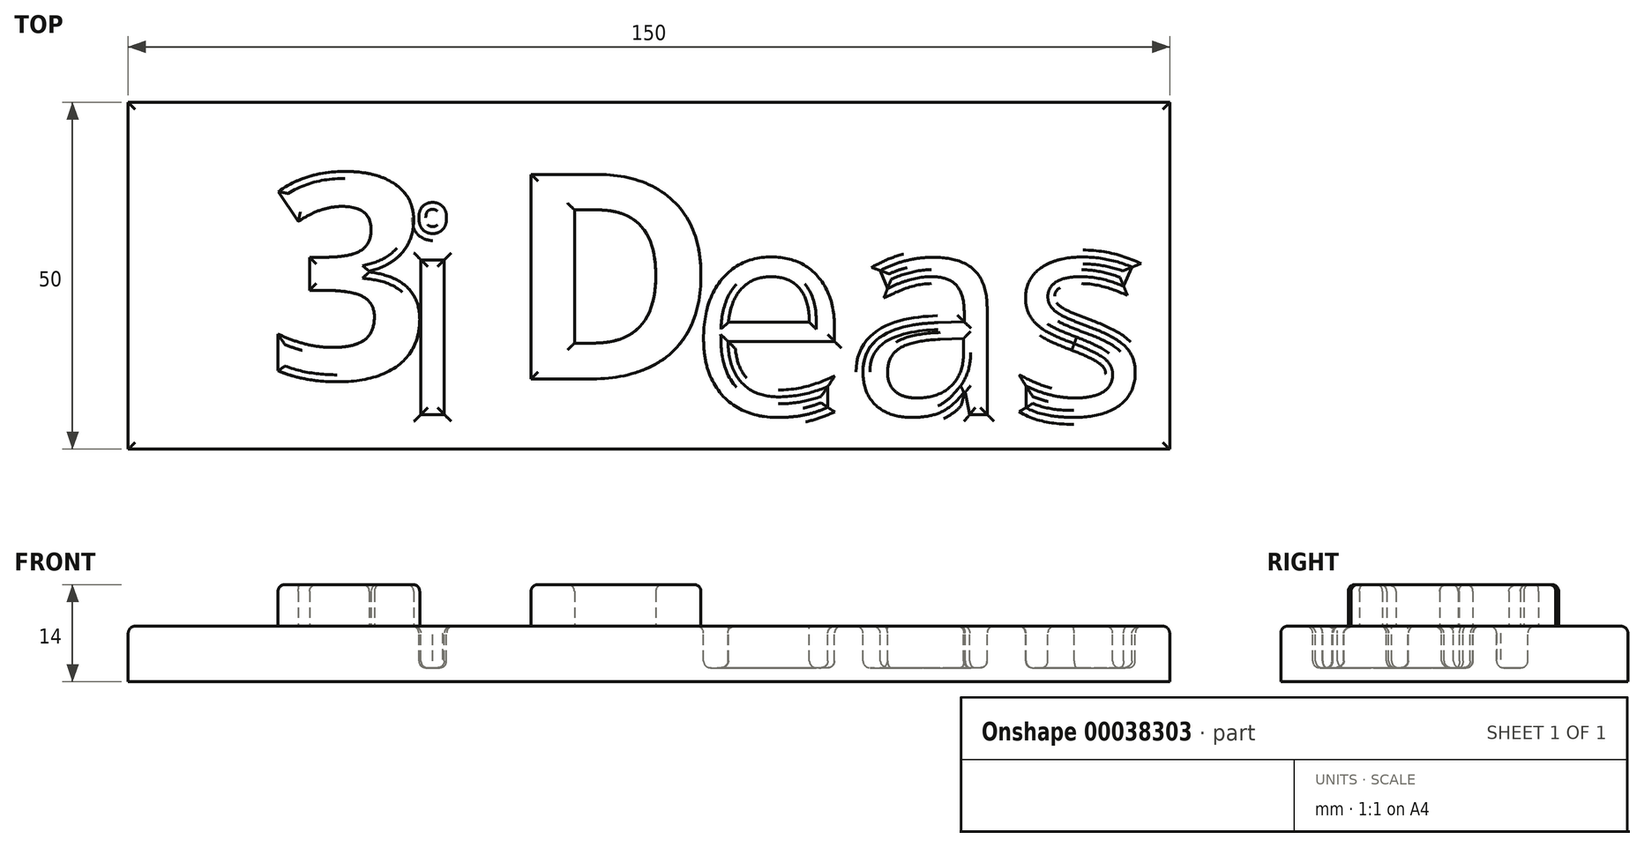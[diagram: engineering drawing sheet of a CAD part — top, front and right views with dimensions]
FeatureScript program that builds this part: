
annotation { "Feature Type Name" : "Feature", "Feature Type Description" : "" }
export const myFeature = defineFeature(function(context is Context, id is Id, definition is map)
    precondition{}
    {
        {
            var Q0;
            Q0=qCreatedBy(makeId("Top.planeOp"),FACE);
            var sketch = newSketch(context, id + "F0", { "sketchPlane" : qUnion([Q0])});
            skLineSegment(sketch, "E0.rect.bottom", {"start": v(-75, 25) * mm, "end": v(75, 25) * mm});
            skLineSegment(sketch, "E0.rect.top", {"start": v(-75, -25) * mm, "end": v(75, -25) * mm});
            skLineSegment(sketch, "E0.rect.left", {"start": v(-75, 25) * mm, "end": v(-75, -25) * mm});
            skLineSegment(sketch, "E0.rect.right", {"start": v(75, 25) * mm, "end": v(75, -25) * mm});
            skPoint(sketch, "E0.rect.middle", {"position": v(0, 0) * mm});
            skSolve(sketch);
        }
        {
            var Q0;
            Q0 = qSketchRegion(id + "F0", true);
            extrude(context, id + "F1", {"entities" : qUnion([Q0]), "depth" : 8 * mm});
        }
        {
            var Q0;
            Q0=makeQuery(id+"F1.opExtrude","CAP_FACE",FACE,{"disambiguationData":[OSD([sQuery(id+"F0.wireOp",EDGE,"E0.rect.bottom"),sQuery(id+"F0.wireOp",EDGE,"E0.rect.top"),sQuery(id+"F0.wireOp",EDGE,"E0.rect.left"),sQuery(id+"F0.wireOp",EDGE,"E0.rect.right")])],"isStart":false});
            var sketch = newSketch(context, id + "F2", { "sketchPlane" : qUnion([Q0])});
            skText(sketch, "E1", { "text": "3 D", "fontName": "OpenSans-Bold.ttf"});
            skPoint(sketch, "E2", {"position": v(-70, 0) * mm});
            const initialGuessF2  = {"E1": [-0.055, -0.01487, 1, 0, 0.02974]};
            skSetInitialGuess(sketch, initialGuessF2);
            skSolve(sketch);
        }
        {
            var Q0;
            Q0 = qSketchRegion(id + "F2", true);
            extrude(context, id + "F3", {"entities" : qUnion([Q0]), "depth" : 6 * mm});
        }
        {
            var Q0;
            Q0=makeQuery(id+"F1.opExtrude","CAP_FACE",FACE,{"disambiguationData":[OSD([sQuery(id+"F0.wireOp",EDGE,"E0.rect.bottom"),sQuery(id+"F0.wireOp",EDGE,"E0.rect.top"),sQuery(id+"F0.wireOp",EDGE,"E0.rect.left"),sQuery(id+"F0.wireOp",EDGE,"E0.rect.right")])],"isStart":false});
            var sketch = newSketch(context, id + "F4", { "sketchPlane" : qUnion([Q0])});
            skText(sketch, "E3", { "text": "i", "fontName": "OpenSans-Regular.ttf"});
            skText(sketch, "E4", { "text": "eas", "fontName": "OpenSans-Regular.ttf"});
            const initialGuessF4  = {"E3": [-0.03643, -0.02, 1, 0, 0.03], "E4": [0.00553, -0.02, 1, 0, 0.03]};
            skSetInitialGuess(sketch, initialGuessF4);
            skSolve(sketch);
        }
        {
            var Q0;
            Q0 = qSketchRegion(id + "F4", true);
            extrude(context, id + "F5", {"entities" : qUnion([Q0]), "operationType" : NewBodyOperationType.REMOVE, "oppositeDirection" : true, "depth" : 6 * mm});
        }
        {
            var Q0;
            Q0=makeQuery(id+"F3.opExtrude","CAP_FACE",FACE,{"disambiguationData":[OSD([sQuery(id+"F2.wireOp",EDGE,"E1.sketch_text.stroke-0"),sQuery(id+"F2.wireOp",EDGE,"E1.sketch_text.stroke-1"),sQuery(id+"F2.wireOp",EDGE,"E1.sketch_text.stroke-2"),sQuery(id+"F2.wireOp",EDGE,"E1.sketch_text.stroke-3"),sQuery(id+"F2.wireOp",EDGE,"E1.sketch_text.stroke-4"),sQuery(id+"F2.wireOp",EDGE,"E1.sketch_text.stroke-5"),sQuery(id+"F2.wireOp",EDGE,"E1.sketch_text.stroke-6"),sQuery(id+"F2.wireOp",EDGE,"E1.sketch_text.stroke-7"),sQuery(id+"F2.wireOp",EDGE,"E1.sketch_text.stroke-8"),sQuery(id+"F2.wireOp",EDGE,"E1.sketch_text.stroke-9"),sQuery(id+"F2.wireOp",EDGE,"E1.sketch_text.stroke-10"),sQuery(id+"F2.wireOp",EDGE,"E1.sketch_text.stroke-11"),sQuery(id+"F2.wireOp",EDGE,"E1.sketch_text.stroke-12"),sQuery(id+"F2.wireOp",EDGE,"E1.sketch_text.stroke-13"),sQuery(id+"F2.wireOp",EDGE,"E1.sketch_text.stroke-14"),sQuery(id+"F2.wireOp",EDGE,"E1.sketch_text.stroke-15"),sQuery(id+"F2.wireOp",EDGE,"E1.sketch_text.stroke-16"),sQuery(id+"F2.wireOp",EDGE,"E1.sketch_text.stroke-17"),sQuery(id+"F2.wireOp",EDGE,"E1.sketch_text.stroke-18"),sQuery(id+"F2.wireOp",EDGE,"E1.sketch_text.stroke-19"),sQuery(id+"F2.wireOp",EDGE,"E1.sketch_text.stroke-20"),sQuery(id+"F2.wireOp",EDGE,"E1.sketch_text.stroke-21"),sQuery(id+"F2.wireOp",EDGE,"E1.sketch_text.stroke-22"),sQuery(id+"F2.wireOp",EDGE,"E1.sketch_text.stroke-23"),sQuery(id+"F2.wireOp",EDGE,"E1.sketch_text.stroke-24"),sQuery(id+"F2.wireOp",EDGE,"E1.sketch_text.stroke-25"),sQuery(id+"F2.wireOp",EDGE,"E1.sketch_text.stroke-26")])],"isStart":false});
            var Q1;
            Q1=makeQuery(id+"F3.opExtrude","CAP_FACE",FACE,{"disambiguationData":[OSD([sQuery(id+"F2.wireOp",EDGE,"E1.sketch_text.stroke-27"),sQuery(id+"F2.wireOp",EDGE,"E1.sketch_text.stroke-28"),sQuery(id+"F2.wireOp",EDGE,"E1.sketch_text.stroke-29"),sQuery(id+"F2.wireOp",EDGE,"E1.sketch_text.stroke-30"),sQuery(id+"F2.wireOp",EDGE,"E1.sketch_text.stroke-31"),sQuery(id+"F2.wireOp",EDGE,"E1.sketch_text.stroke-32"),sQuery(id+"F2.wireOp",EDGE,"E1.sketch_text.stroke-33"),sQuery(id+"F2.wireOp",EDGE,"E1.sketch_text.stroke-34"),sQuery(id+"F2.wireOp",EDGE,"E1.sketch_text.stroke-35"),sQuery(id+"F2.wireOp",EDGE,"E1.sketch_text.stroke-36"),sQuery(id+"F2.wireOp",EDGE,"E1.sketch_text.stroke-37"),sQuery(id+"F2.wireOp",EDGE,"E1.sketch_text.stroke-38")])],"isStart":false});
            var Q2;
            Q2=makeQuery(id+"F5.boolean.opBoolean","COPY",FACE,{"derivedFrom":makeQuery(id+"F5.opExtrude","CAP_FACE",FACE,{"disambiguationData":[OSD([sQuery(id+"F4.wireOp",EDGE,"E4.sketch_text.stroke-0"),sQuery(id+"F4.wireOp",EDGE,"E4.sketch_text.stroke-1"),sQuery(id+"F4.wireOp",EDGE,"E4.sketch_text.stroke-2"),sQuery(id+"F4.wireOp",EDGE,"E4.sketch_text.stroke-3"),sQuery(id+"F4.wireOp",EDGE,"E4.sketch_text.stroke-4"),sQuery(id+"F4.wireOp",EDGE,"E4.sketch_text.stroke-5"),sQuery(id+"F4.wireOp",EDGE,"E4.sketch_text.stroke-6"),sQuery(id+"F4.wireOp",EDGE,"E4.sketch_text.stroke-7"),sQuery(id+"F4.wireOp",EDGE,"E4.sketch_text.stroke-8"),sQuery(id+"F4.wireOp",EDGE,"E4.sketch_text.stroke-9"),sQuery(id+"F4.wireOp",EDGE,"E4.sketch_text.stroke-10"),sQuery(id+"F4.wireOp",EDGE,"E4.sketch_text.stroke-11"),sQuery(id+"F4.wireOp",EDGE,"E4.sketch_text.stroke-12"),sQuery(id+"F4.wireOp",EDGE,"E4.sketch_text.stroke-13"),sQuery(id+"F4.wireOp",EDGE,"E4.sketch_text.stroke-14"),sQuery(id+"F4.wireOp",EDGE,"E4.sketch_text.stroke-15"),sQuery(id+"F4.wireOp",EDGE,"E4.sketch_text.stroke-16"),sQuery(id+"F4.wireOp",EDGE,"E4.sketch_text.stroke-17"),sQuery(id+"F4.wireOp",EDGE,"E4.sketch_text.stroke-18")])],"isStart":false})});
            var Q3;
            Q3=makeQuery(id+"F5.boolean.opBoolean","COPY",FACE,{"derivedFrom":makeQuery(id+"F5.opExtrude","CAP_FACE",FACE,{"disambiguationData":[OSD([sQuery(id+"F4.wireOp",EDGE,"E4.sketch_text.stroke-46"),sQuery(id+"F4.wireOp",EDGE,"E4.sketch_text.stroke-47"),sQuery(id+"F4.wireOp",EDGE,"E4.sketch_text.stroke-48"),sQuery(id+"F4.wireOp",EDGE,"E4.sketch_text.stroke-49"),sQuery(id+"F4.wireOp",EDGE,"E4.sketch_text.stroke-50"),sQuery(id+"F4.wireOp",EDGE,"E4.sketch_text.stroke-51"),sQuery(id+"F4.wireOp",EDGE,"E4.sketch_text.stroke-52"),sQuery(id+"F4.wireOp",EDGE,"E4.sketch_text.stroke-53"),sQuery(id+"F4.wireOp",EDGE,"E4.sketch_text.stroke-54"),sQuery(id+"F4.wireOp",EDGE,"E4.sketch_text.stroke-55"),sQuery(id+"F4.wireOp",EDGE,"E4.sketch_text.stroke-56"),sQuery(id+"F4.wireOp",EDGE,"E4.sketch_text.stroke-57"),sQuery(id+"F4.wireOp",EDGE,"E4.sketch_text.stroke-58"),sQuery(id+"F4.wireOp",EDGE,"E4.sketch_text.stroke-59"),sQuery(id+"F4.wireOp",EDGE,"E4.sketch_text.stroke-60"),sQuery(id+"F4.wireOp",EDGE,"E4.sketch_text.stroke-61"),sQuery(id+"F4.wireOp",EDGE,"E4.sketch_text.stroke-62"),sQuery(id+"F4.wireOp",EDGE,"E4.sketch_text.stroke-63"),sQuery(id+"F4.wireOp",EDGE,"E4.sketch_text.stroke-64"),sQuery(id+"F4.wireOp",EDGE,"E4.sketch_text.stroke-65"),sQuery(id+"F4.wireOp",EDGE,"E4.sketch_text.stroke-66"),sQuery(id+"F4.wireOp",EDGE,"E4.sketch_text.stroke-67"),sQuery(id+"F4.wireOp",EDGE,"E4.sketch_text.stroke-68"),sQuery(id+"F4.wireOp",EDGE,"E4.sketch_text.stroke-69"),sQuery(id+"F4.wireOp",EDGE,"E4.sketch_text.stroke-70")])],"isStart":false})});
            var Q4;
            Q4=makeQuery(id+"F5.boolean.opBoolean","COPY",FACE,{"derivedFrom":makeQuery(id+"F5.opExtrude","CAP_FACE",FACE,{"disambiguationData":[OSD([sQuery(id+"F4.wireOp",EDGE,"E3.sketch_text.stroke-0"),sQuery(id+"F4.wireOp",EDGE,"E3.sketch_text.stroke-1"),sQuery(id+"F4.wireOp",EDGE,"E3.sketch_text.stroke-2"),sQuery(id+"F4.wireOp",EDGE,"E3.sketch_text.stroke-3")])],"isStart":false})});
            var Q5;
            Q5=makeQuery(id+"F5.boolean.opBoolean","COPY",FACE,{"derivedFrom":makeQuery(id+"F5.opExtrude","CAP_FACE",FACE,{"disambiguationData":[OSD([sQuery(id+"F4.wireOp",EDGE,"E3.sketch_text.stroke-4"),sQuery(id+"F4.wireOp",EDGE,"E3.sketch_text.stroke-5"),sQuery(id+"F4.wireOp",EDGE,"E3.sketch_text.stroke-6"),sQuery(id+"F4.wireOp",EDGE,"E3.sketch_text.stroke-7"),sQuery(id+"F4.wireOp",EDGE,"E3.sketch_text.stroke-8"),sQuery(id+"F4.wireOp",EDGE,"E3.sketch_text.stroke-9"),sQuery(id+"F4.wireOp",EDGE,"E3.sketch_text.stroke-10"),sQuery(id+"F4.wireOp",EDGE,"E3.sketch_text.stroke-11")])],"isStart":false})});
            var Q6;
            {var subQ0=sQuery(id+"F0.wireOp",EDGE,"E0.rect.bottom");var subQ1=sQuery(id+"F0.wireOp",EDGE,"E0.rect.top");var subQ2=sQuery(id+"F0.wireOp",EDGE,"E0.rect.left");var subQ3=sQuery(id+"F0.wireOp",EDGE,"E0.rect.right");Q6=makeQuery(id+"F5.boolean.opBoolean","SPLIT",FACE,{"disambiguationData":[TD([makeQuery(id+"F1.opExtrude","SWEPT_FACE",FACE,{"disambiguationData":[OSD([subQ0])]})])],"derivedFrom":makeQuery(id+"F1.opExtrude","CAP_FACE",FACE,{"disambiguationData":[OSD([subQ0,subQ1,subQ2,subQ3])],"isStart":false})});}
            var Q7;
            Q7=makeQuery(id+"F5.boolean.opBoolean","COPY",FACE,{"derivedFrom":makeQuery(id+"F5.opExtrude","CAP_FACE",FACE,{"disambiguationData":[OSD([sQuery(id+"F4.wireOp",EDGE,"E4.sketch_text.stroke-19"),sQuery(id+"F4.wireOp",EDGE,"E4.sketch_text.stroke-20"),sQuery(id+"F4.wireOp",EDGE,"E4.sketch_text.stroke-21"),sQuery(id+"F4.wireOp",EDGE,"E4.sketch_text.stroke-22"),sQuery(id+"F4.wireOp",EDGE,"E4.sketch_text.stroke-23"),sQuery(id+"F4.wireOp",EDGE,"E4.sketch_text.stroke-24"),sQuery(id+"F4.wireOp",EDGE,"E4.sketch_text.stroke-25"),sQuery(id+"F4.wireOp",EDGE,"E4.sketch_text.stroke-26"),sQuery(id+"F4.wireOp",EDGE,"E4.sketch_text.stroke-27"),sQuery(id+"F4.wireOp",EDGE,"E4.sketch_text.stroke-28"),sQuery(id+"F4.wireOp",EDGE,"E4.sketch_text.stroke-29"),sQuery(id+"F4.wireOp",EDGE,"E4.sketch_text.stroke-30"),sQuery(id+"F4.wireOp",EDGE,"E4.sketch_text.stroke-31"),sQuery(id+"F4.wireOp",EDGE,"E4.sketch_text.stroke-32"),sQuery(id+"F4.wireOp",EDGE,"E4.sketch_text.stroke-33"),sQuery(id+"F4.wireOp",EDGE,"E4.sketch_text.stroke-34"),sQuery(id+"F4.wireOp",EDGE,"E4.sketch_text.stroke-35"),sQuery(id+"F4.wireOp",EDGE,"E4.sketch_text.stroke-36"),sQuery(id+"F4.wireOp",EDGE,"E4.sketch_text.stroke-37"),sQuery(id+"F4.wireOp",EDGE,"E4.sketch_text.stroke-38"),sQuery(id+"F4.wireOp",EDGE,"E4.sketch_text.stroke-39"),sQuery(id+"F4.wireOp",EDGE,"E4.sketch_text.stroke-40"),sQuery(id+"F4.wireOp",EDGE,"E4.sketch_text.stroke-41"),sQuery(id+"F4.wireOp",EDGE,"E4.sketch_text.stroke-42"),sQuery(id+"F4.wireOp",EDGE,"E4.sketch_text.stroke-43"),sQuery(id+"F4.wireOp",EDGE,"E4.sketch_text.stroke-44"),sQuery(id+"F4.wireOp",EDGE,"E4.sketch_text.stroke-45")])],"isStart":false})});
            fillet(context, id + "F6", {"entities" : qUnion([Q0, Q1, Q2, Q3, Q4, Q5, Q6, Q7]), "radius" : 1 * mm, "tangentPropagation" : true, "allowEdgeOverflow" : false});
        }
    });
